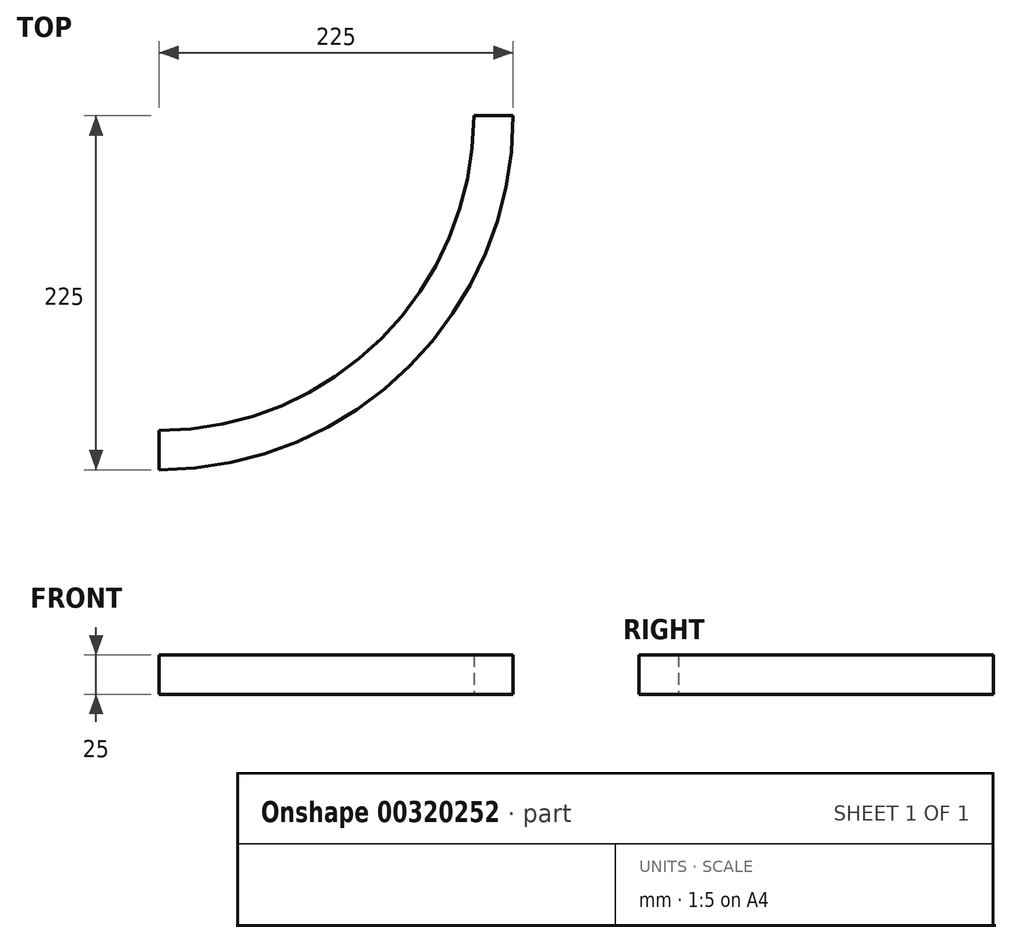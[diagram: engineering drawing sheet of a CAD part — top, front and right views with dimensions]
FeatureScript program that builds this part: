
annotation { "Feature Type Name" : "Feature", "Feature Type Description" : "" }
export const myFeature = defineFeature(function(context is Context, id is Id, definition is map)
    precondition{}
    {
        {
            var Q0;
            Q0=qCreatedBy(makeId("Top.planeOp"),FACE);
            var sketch = newSketch(context, id + "F0", { "sketchPlane" : qUnion([Q0])});
            skArc(sketch, "E0", {"start": v(0, 0) * mm, "mid": v(159.1, 65.9) * mm, "end": v(225, 225) * mm});
            skArc(sketch, "E1", {"start": v(0, 25) * mm, "mid": v(141.42, 83.58) * mm, "end": v(200, 225) * mm});
            skLineSegment(sketch, "E2", {"start": v(0, 25) * mm, "end": v(0, 0) * mm});
            skLineSegment(sketch, "E3", {"start": v(200, 225) * mm, "end": v(225, 225) * mm});
            skSolve(sketch);
        }
        {
            var Q0;
            Q0=makeQuery(id+"F0.imprint","IMPRINT",FACE,{"disambiguationData":[TD([[makeQuery(id+"F0.imprint","IMPRINT",EDGE,{"derivedFrom":sQuery(id+"F0.wireOp",EDGE,"E0")}),1.0]])]});
            extrude(context, id + "F1", {"entities" : qUnion([Q0]), "endBound" : BoundingType.SYMMETRIC, "depth" : 25 * mm});
        }
    });
